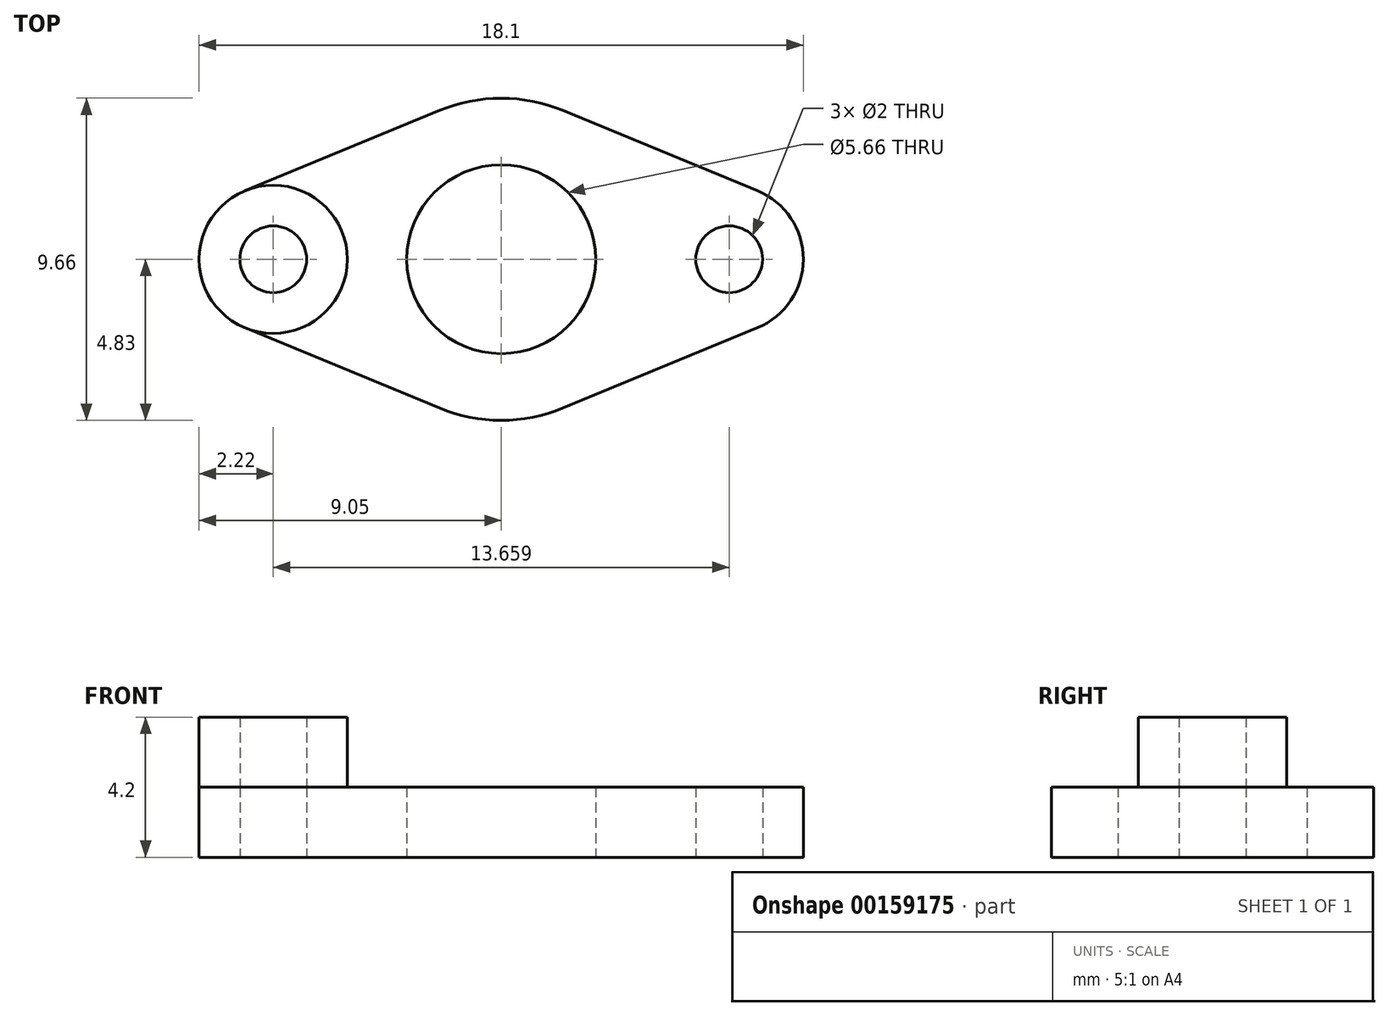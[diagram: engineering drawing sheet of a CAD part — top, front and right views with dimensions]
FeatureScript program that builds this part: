
annotation { "Feature Type Name" : "Feature", "Feature Type Description" : "" }
export const myFeature = defineFeature(function(context is Context, id is Id, definition is map)
    precondition{}
    {
        {
            var Q0;
            Q0=qCreatedBy(makeId("Top.planeOp"),FACE);
            var sketch = newSketch(context, id + "F0", { "sketchPlane" : qUnion([Q0])});
            skCircle(sketch, "E0", {"center": v(0, 0) * mm, "radius": 2.83 * mm});
            skCircle(sketch, "E1", {"center": v(-6.83, 0) * mm, "radius": 1 * mm});
            skCircle(sketch, "E2", {"center": v(6.83, 0) * mm, "radius": 1 * mm});
            skLineSegment(sketch, "E3", {"start": v(-7.68, 2.05) * mm, "end": v(-1.84, 4.46) * mm});
            skLineSegment(sketch, "E4", {"start": v(1.84, 4.46) * mm, "end": v(7.68, 2.05) * mm});
            skLineSegment(sketch, "E5", {"start": v(7.68, -2.05) * mm, "end": v(1.84, -4.46) * mm});
            skLineSegment(sketch, "E6", {"start": v(-1.84, -4.46) * mm, "end": v(-7.68, -2.05) * mm});
            skPoint(sketch, "E7.visualSharp", {"position": v(0, 5.23) * mm});
            skArc(sketch, "E7.filletArc", {"start": v(1.84, 4.46) * mm, "mid": v(0, 4.83) * mm, "end": v(-1.84, 4.46) * mm});
            skPoint(sketch, "E8.visualSharp", {"position": v(0, -5.23) * mm});
            skArc(sketch, "E8.filletArc", {"start": v(-1.84, -4.46) * mm, "mid": v(0, -4.83) * mm, "end": v(1.84, -4.46) * mm});
            skPoint(sketch, "E9.visualSharp", {"position": v(-12.64, 0) * mm});
            skArc(sketch, "E9.filletArc", {"start": v(-7.68, 2.05) * mm, "mid": v(-9.05, 0) * mm, "end": v(-7.68, -2.05) * mm});
            skPoint(sketch, "E10.visualSharp", {"position": v(12.64, 0) * mm});
            skArc(sketch, "E10.filletArc", {"start": v(7.68, -2.05) * mm, "mid": v(9.05, 0) * mm, "end": v(7.68, 2.05) * mm});
            skSolve(sketch);
        }
        {
            var Q0;
            Q0=makeQuery(id+"F0.imprint","IMPRINT",FACE,{"disambiguationData":[TD([[makeQuery(id+"F0.imprint","IMPRINT",EDGE,{"derivedFrom":sQuery(id+"F0.wireOp",EDGE,"E0")}),-1.0]])]});
            extrude(context, id + "F1", {"entities" : qUnion([Q0]), "depth" : 2.1 * mm});
        }
        {
            var Q0;
            Q0=makeQuery(id+"F1.opExtrude","CAP_FACE",FACE,{"disambiguationData":[OSD([sQuery(id+"F0.wireOp",EDGE,"E0"),sQuery(id+"F0.wireOp",EDGE,"E1"),sQuery(id+"F0.wireOp",EDGE,"E2"),sQuery(id+"F0.wireOp",EDGE,"E3"),sQuery(id+"F0.wireOp",EDGE,"E4"),sQuery(id+"F0.wireOp",EDGE,"E5"),sQuery(id+"F0.wireOp",EDGE,"E6"),sQuery(id+"F0.wireOp",EDGE,"E7.filletArc"),sQuery(id+"F0.wireOp",EDGE,"E8.filletArc"),sQuery(id+"F0.wireOp",EDGE,"E9.filletArc"),sQuery(id+"F0.wireOp",EDGE,"E10.filletArc")])],"isStart":false});
            var sketch = newSketch(context, id + "F2", { "sketchPlane" : qUnion([Q0])});
            skCircle(sketch, "E11.0", {"center": v(-6.83, 0) * mm, "radius": 1 * mm});
            skCircle(sketch, "E12", {"center": v(-6.83, 0) * mm, "radius": 2.22 * mm});
            skSolve(sketch);
        }
        {
            var Q0;
            Q0=makeQuery(id+"F2.imprint","IMPRINT",FACE,{"disambiguationData":[TD([[makeQuery(id+"F2.imprint","IMPRINT",EDGE,{"derivedFrom":sQuery(id+"F2.wireOp",EDGE,"E11.0")}),-1.0]])]});
            extrude(context, id + "F3", {"entities" : qUnion([Q0]), "depth" : 2.1 * mm});
        }
    });
